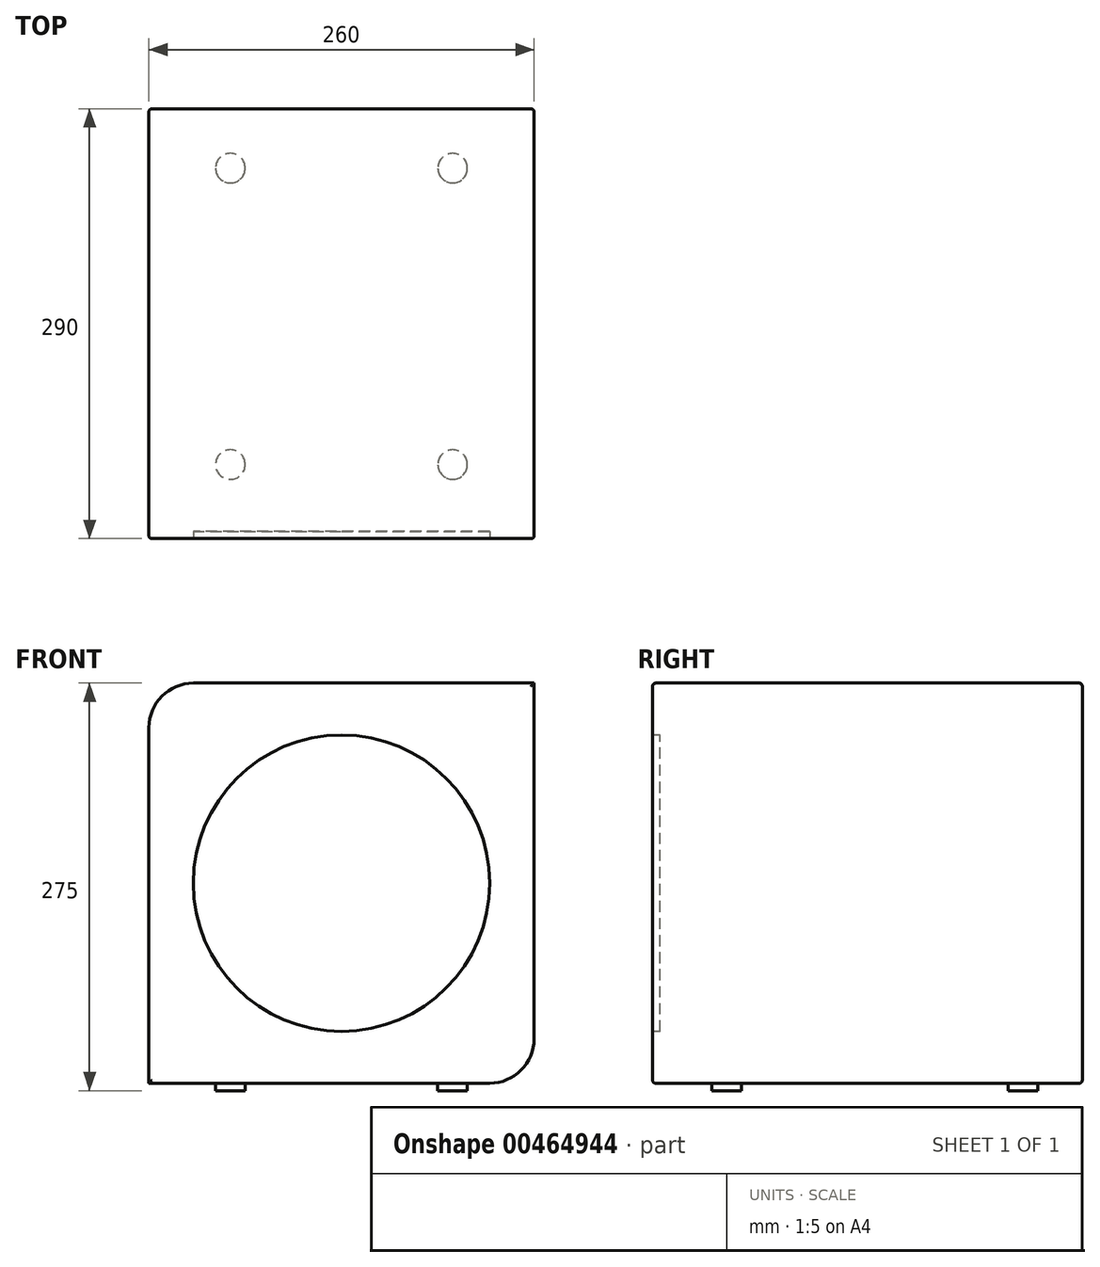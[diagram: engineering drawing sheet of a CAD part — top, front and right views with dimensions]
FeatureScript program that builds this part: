
annotation { "Feature Type Name" : "Feature", "Feature Type Description" : "" }
export const myFeature = defineFeature(function(context is Context, id is Id, definition is map)
    precondition{}
    {
        {
            var Q0;
            Q0=qCreatedBy(makeId("Front.planeOp"),FACE);
            var sketch = newSketch(context, id + "F0", { "sketchPlane" : qUnion([Q0])});
            skLineSegment(sketch, "E0.bottom", {"start": v(100, -135) * mm, "end": v(-130, -135) * mm});
            skLineSegment(sketch, "E0.top", {"start": v(130, 135) * mm, "end": v(-100, 135) * mm});
            skLineSegment(sketch, "E0.left", {"start": v(130, -105) * mm, "end": v(130, 135) * mm});
            skLineSegment(sketch, "E0.right", {"start": v(-130, -135) * mm, "end": v(-130, 105) * mm});
            skPoint(sketch, "E0.middle", {"position": v(0, 0) * mm});
            skPoint(sketch, "E1.visualSharp", {"position": v(-130, 135) * mm});
            skArc(sketch, "E1.filletArc", {"start": v(-100, 135) * mm, "mid": v(-121.21, 126.21) * mm, "end": v(-130, 105) * mm});
            skPoint(sketch, "E2.visualSharp", {"position": v(130, -135) * mm});
            skArc(sketch, "E2.filletArc", {"start": v(100, -135) * mm, "mid": v(121.21, -126.21) * mm, "end": v(130, -105) * mm});
            skSolve(sketch);
        }
        {
            var Q0;
            Q0 = qSketchRegion(id + "F0", true);
            extrude(context, id + "F1", {"entities" : qUnion([Q0]), "oppositeDirection" : true, "depth" : 290 * mm});
        }
        {
            var Q0;
            Q0=makeQuery(id+"F1.opExtrude","SWEPT_FACE",FACE,{"disambiguationData":[OSD([sQuery(id+"F0.wireOp",EDGE,"E0.bottom")])]});
            var sketch = newSketch(context, id + "F2", { "sketchPlane" : qUnion([Q0])});
            skLineSegment(sketch, "E3.bottom", {"start": v(-75, -250) * mm, "end": v(75, -250) * mm, "construction": true});
            skLineSegment(sketch, "E3.top", {"start": v(-75, -50) * mm, "end": v(75, -50) * mm, "construction": true});
            skLineSegment(sketch, "E3.left", {"start": v(-75, -250) * mm, "end": v(-75, -50) * mm, "construction": true});
            skLineSegment(sketch, "E3.right", {"start": v(75, -250) * mm, "end": v(75, -50) * mm, "construction": true});
            skPoint(sketch, "E3.middle", {"position": v(0, -150) * mm});
            skCircle(sketch, "E4", {"center": v(-75, -50) * mm, "radius": 10 * mm});
            skCircle(sketch, "E5", {"center": v(75, -50) * mm, "radius": 10 * mm});
            skCircle(sketch, "E6", {"center": v(75, -250) * mm, "radius": 10 * mm});
            skCircle(sketch, "E7", {"center": v(-75, -250) * mm, "radius": 10 * mm});
            skSolve(sketch);
        }
        {
            var Q0;
            Q0 = qSketchRegion(id + "F2", true);
            extrude(context, id + "F3", {"entities" : qUnion([Q0]), "operationType" : NewBodyOperationType.ADD, "depth" : 5 * mm});
        }
        {
            var Q0;
            Q0=makeQuery(id+"F1.opExtrude","CAP_FACE",FACE,{"disambiguationData":[OSD([sQuery(id+"F0.wireOp",EDGE,"E0.bottom"),sQuery(id+"F0.wireOp",EDGE,"E0.top"),sQuery(id+"F0.wireOp",EDGE,"E0.left"),sQuery(id+"F0.wireOp",EDGE,"E0.right"),sQuery(id+"F0.wireOp",EDGE,"E1.filletArc"),sQuery(id+"F0.wireOp",EDGE,"E2.filletArc")])],"isStart":true});
            var Q1;
            Q1=makeQuery(id+"F1.opExtrude","CAP_FACE",FACE,{"disambiguationData":[OSD([sQuery(id+"F0.wireOp",EDGE,"E0.bottom"),sQuery(id+"F0.wireOp",EDGE,"E0.top"),sQuery(id+"F0.wireOp",EDGE,"E0.left"),sQuery(id+"F0.wireOp",EDGE,"E0.right"),sQuery(id+"F0.wireOp",EDGE,"E1.filletArc"),sQuery(id+"F0.wireOp",EDGE,"E2.filletArc")])],"isStart":false});
            fillet(context, id + "F4", {"entities" : qUnion([Q0, Q1]), "radius" : 2 * mm, "tangentPropagation" : true, "allowEdgeOverflow" : false});
        }
        {
            var Q0;
            Q0=makeQuery(id+"F1.opExtrude","CAP_FACE",FACE,{"disambiguationData":[OSD([sQuery(id+"F0.wireOp",EDGE,"E0.bottom"),sQuery(id+"F0.wireOp",EDGE,"E0.top"),sQuery(id+"F0.wireOp",EDGE,"E0.left"),sQuery(id+"F0.wireOp",EDGE,"E0.right"),sQuery(id+"F0.wireOp",EDGE,"E1.filletArc"),sQuery(id+"F0.wireOp",EDGE,"E2.filletArc")])],"isStart":true});
            var sketch = newSketch(context, id + "F5", { "sketchPlane" : qUnion([Q0])});
            skCircle(sketch, "E8", {"center": v(0, 0) * mm, "radius": 100 * mm});
            skSolve(sketch);
        }
        {
            var Q0;
            Q0 = qSketchRegion(id + "F5", true);
            extrude(context, id + "F6", {"entities" : qUnion([Q0]), "operationType" : NewBodyOperationType.REMOVE, "oppositeDirection" : true, "depth" : 5 * mm});
        }
    });
